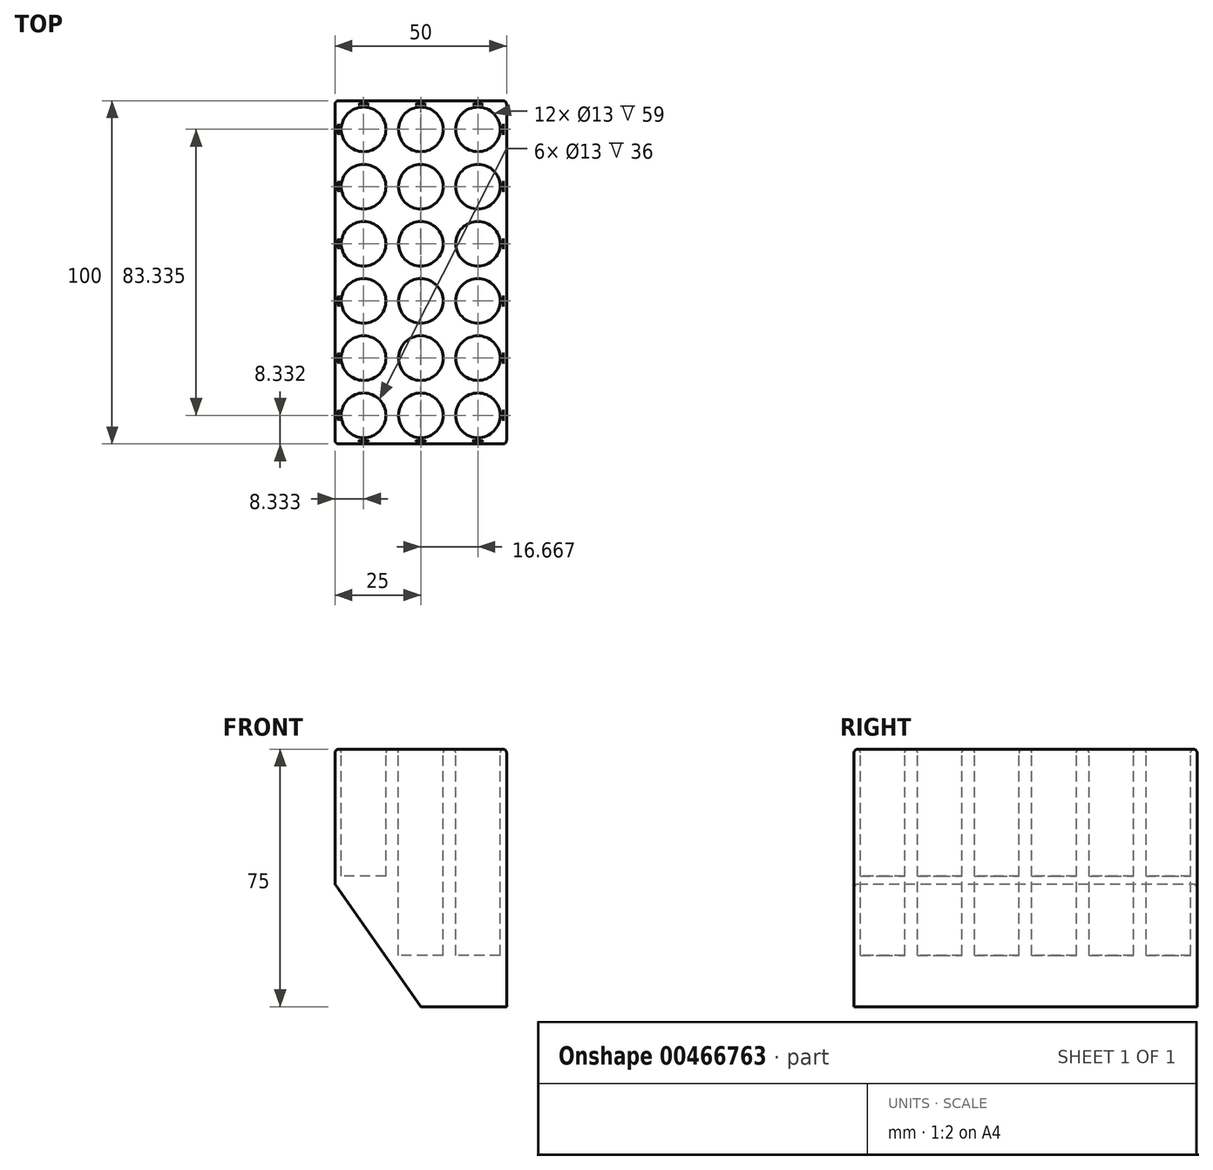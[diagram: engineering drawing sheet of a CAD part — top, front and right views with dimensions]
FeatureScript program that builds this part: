
annotation { "Feature Type Name" : "Feature", "Feature Type Description" : "" }
export const myFeature = defineFeature(function(context is Context, id is Id, definition is map)
    precondition{}
    {
        {
            var Q0;
            Q0=qCreatedBy(makeId("Front.planeOp"),FACE);
            var sketch = newSketch(context, id + "F0", { "sketchPlane" : qUnion([Q0])});
            skLineSegment(sketch, "E0.bottom", {"start": v(25, 0) * mm, "end": v(50, 0) * mm});
            skLineSegment(sketch, "E0.top", {"start": v(0, 75) * mm, "end": v(50, 75) * mm});
            skLineSegment(sketch, "E0.left", {"start": v(0, 35.7) * mm, "end": v(0, 75) * mm});
            skLineSegment(sketch, "E0.right", {"start": v(50, 0) * mm, "end": v(50, 75) * mm});
            skLineSegment(sketch, "E1", {"start": v(0, 35.7) * mm, "end": v(25, 0) * mm});
            skPoint(sketch, "E2.orphan", {"position": v(0, 0) * mm});
            skSolve(sketch);
        }
        {
            var Q0;
            Q0 = qSketchRegion(id + "F0", true);
            extrude(context, id + "F1", {"entities" : qUnion([Q0]), "depth" : 100 * mm});
        }
        {
            var Q0;
            Q0=makeQuery(id+"F1.opExtrude","SWEPT_FACE",FACE,{"disambiguationData":[OSD([sQuery(id+"F0.wireOp",EDGE,"E0.top")])]});
            var sketch = newSketch(context, id + "F2", { "sketchPlane" : qUnion([Q0])});
            skCircle(sketch, "E3", {"center": v(41.67, -8.33) * mm, "radius": 6.5 * mm});
            skCircle(sketch, "E4.0.1.0", {"center": v(41.67, -25) * mm, "radius": 6.5 * mm});
            skCircle(sketch, "E4.0.2.0", {"center": v(41.67, -41.67) * mm, "radius": 6.5 * mm});
            skCircle(sketch, "E4.0.3.0", {"center": v(41.67, -58.33) * mm, "radius": 6.5 * mm});
            skCircle(sketch, "E4.0.4.0", {"center": v(41.67, -75) * mm, "radius": 6.5 * mm});
            skCircle(sketch, "E4.0.5.0", {"center": v(41.67, -91.67) * mm, "radius": 6.5 * mm});
            skLineSegment(sketch, "E4.direction1", {"start": v(41.67, -8.33) * mm, "end": v(25, -8.33) * mm, "construction": true});
            skLineSegment(sketch, "E4.direction2", {"start": v(41.67, -8.33) * mm, "end": v(41.67, -25) * mm, "construction": true});
            skSolve(sketch);
        }
        {
            var Q0;
            Q0 = qSketchRegion(id + "F2", true);
            extrude(context, id + "F3", {"entities" : qUnion([Q0]), "operationType" : NewBodyOperationType.REMOVE, "oppositeDirection" : true, "depth" : 60 * mm});
        }
        {
            var Q0;
            Q0=makeQuery(id+"F1.opExtrude","SWEPT_FACE",FACE,{"disambiguationData":[OSD([sQuery(id+"F0.wireOp",EDGE,"E0.top")])]});
            var sketch = newSketch(context, id + "F4", { "sketchPlane" : qUnion([Q0])});
            skCircle(sketch, "E5", {"center": v(25, -8.33) * mm, "radius": 6.5 * mm});
            skCircle(sketch, "E6.0.1.0", {"center": v(25, -25) * mm, "radius": 6.5 * mm});
            skCircle(sketch, "E6.0.2.0", {"center": v(25, -41.67) * mm, "radius": 6.5 * mm});
            skCircle(sketch, "E6.0.3.0", {"center": v(25, -58.33) * mm, "radius": 6.5 * mm});
            skCircle(sketch, "E6.0.4.0", {"center": v(25, -75) * mm, "radius": 6.5 * mm});
            skCircle(sketch, "E6.0.5.0", {"center": v(25, -91.67) * mm, "radius": 6.5 * mm});
            skLineSegment(sketch, "E6.direction1", {"start": v(25, -8.33) * mm, "end": v(50, -8.33) * mm, "construction": true});
            skLineSegment(sketch, "E6.direction2", {"start": v(25, -8.33) * mm, "end": v(25, -25) * mm, "construction": true});
            skSolve(sketch);
        }
        {
            var Q0;
            Q0 = qSketchRegion(id + "F4", true);
            extrude(context, id + "F5", {"entities" : qUnion([Q0]), "operationType" : NewBodyOperationType.REMOVE, "oppositeDirection" : true, "depth" : 60 * mm});
        }
        {
            var Q0;
            Q0=makeQuery(id+"F1.opExtrude","SWEPT_FACE",FACE,{"disambiguationData":[OSD([sQuery(id+"F0.wireOp",EDGE,"E0.top")])]});
            var sketch = newSketch(context, id + "F6", { "sketchPlane" : qUnion([Q0])});
            skCircle(sketch, "E7", {"center": v(8.33, -8.33) * mm, "radius": 6.5 * mm});
            skCircle(sketch, "E8.0.1.0", {"center": v(8.33, -25) * mm, "radius": 6.5 * mm});
            skCircle(sketch, "E8.0.2.0", {"center": v(8.33, -41.67) * mm, "radius": 6.5 * mm});
            skCircle(sketch, "E8.0.3.0", {"center": v(8.33, -58.33) * mm, "radius": 6.5 * mm});
            skCircle(sketch, "E8.0.4.0", {"center": v(8.33, -75) * mm, "radius": 6.5 * mm});
            skCircle(sketch, "E8.0.5.0", {"center": v(8.33, -91.67) * mm, "radius": 6.5 * mm});
            skLineSegment(sketch, "E8.direction1", {"start": v(8.33, -8.33) * mm, "end": v(33.33, -8.33) * mm, "construction": true});
            skLineSegment(sketch, "E8.direction2", {"start": v(8.33, -8.33) * mm, "end": v(8.33, -25) * mm, "construction": true});
            skSolve(sketch);
        }
        {
            var Q0;
            Q0 = qSketchRegion(id + "F6", true);
            extrude(context, id + "F7", {"entities" : qUnion([Q0]), "operationType" : NewBodyOperationType.REMOVE, "oppositeDirection" : true, "depth" : 37 * mm});
        }
        {
            var Q0;
            Q0=makeQuery(id+"F1.opExtrude","SWEPT_FACE",FACE,{"disambiguationData":[OSD([sQuery(id+"F0.wireOp",EDGE,"E0.top")])]});
            var Q1;
            Q1=makeQuery(id+"F1.opExtrude","CAP_EDGE",EDGE,{"disambiguationData":[OSD([sQuery(id+"F0.wireOp",EDGE,"E0.right")])],"isStart":false});
            var Q2;
            Q2=makeQuery(id+"F1.opExtrude","CAP_EDGE",EDGE,{"disambiguationData":[OSD([sQuery(id+"F0.wireOp",EDGE,"E0.left")])],"isStart":false});
            var Q3;
            Q3=makeQuery(id+"F1.opExtrude","CAP_EDGE",EDGE,{"disambiguationData":[OSD([sQuery(id+"F0.wireOp",EDGE,"E0.right")])],"isStart":true});
            var Q4;
            Q4=makeQuery(id+"F1.opExtrude","CAP_EDGE",EDGE,{"disambiguationData":[OSD([sQuery(id+"F0.wireOp",EDGE,"E0.left")])],"isStart":true});
            fillet(context, id + "F8", {"entities" : qUnion([Q0, Q1, Q2, Q3, Q4]), "radius" : 1 * mm, "tangentPropagation" : true, "allowEdgeOverflow" : false});
        }
    });
